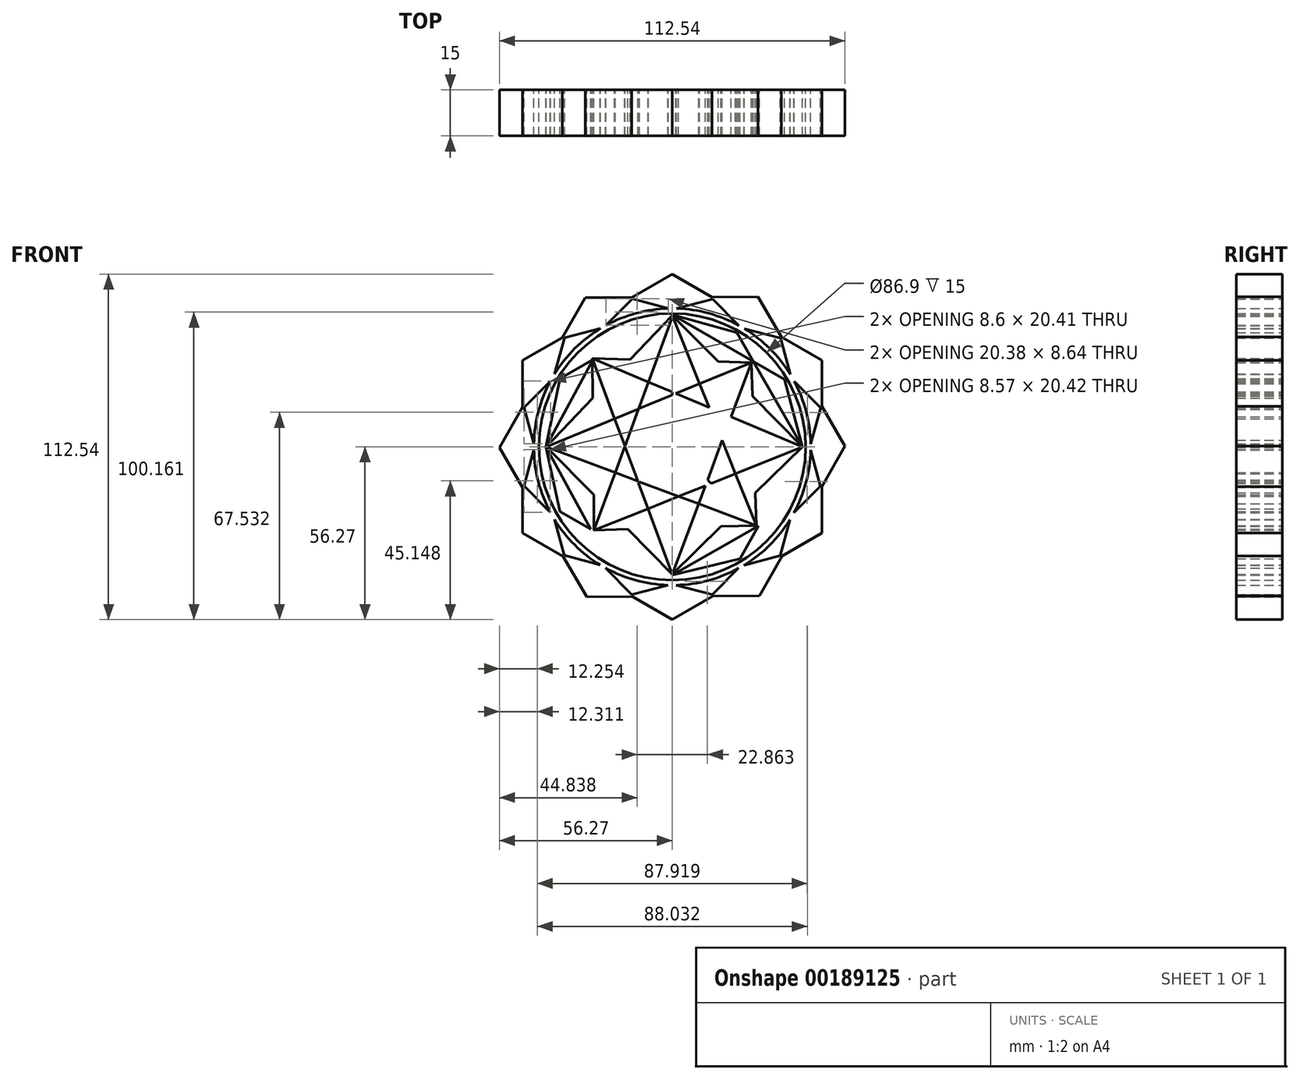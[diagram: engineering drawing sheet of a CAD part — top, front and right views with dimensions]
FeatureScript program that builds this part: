
annotation { "Feature Type Name" : "Feature", "Feature Type Description" : "" }
export const myFeature = defineFeature(function(context is Context, id is Id, definition is map)
    precondition{}
    {
        {
            var Q0;
            Q0=qCreatedBy(makeId("Front.planeOp"),FACE);
            var sketch = newSketch(context, id + "F0", { "sketchPlane" : qUnion([Q0])});
            skCircle(sketch, "E0.cCircle", {"center": v(0, 0) * mm, "radius": 48.73 * mm, "construction": true});
            skLineSegment(sketch, "E0.0", {"start": v(-48.73, -28.13) * mm, "end": v(-48.73, 28.13) * mm});
            skLineSegment(sketch, "E0.1", {"start": v(-48.73, 28.13) * mm, "end": v(0, 56.27) * mm});
            skLineSegment(sketch, "E0.2", {"start": v(0, 56.27) * mm, "end": v(48.73, 28.13) * mm});
            skLineSegment(sketch, "E0.3", {"start": v(48.73, 28.13) * mm, "end": v(48.73, -28.13) * mm});
            skLineSegment(sketch, "E0.4", {"start": v(48.73, -28.13) * mm, "end": v(0, -56.27) * mm});
            skLineSegment(sketch, "E0.5", {"start": v(0, -56.27) * mm, "end": v(-48.73, -28.13) * mm});
            skPoint(sketch, "E0.0.midPoint", {"position": v(-48.73, 0) * mm});
            skLineSegment(sketch, "E1.0", {"start": v(-56.27, -0.3) * mm, "end": v(-28.4, 48.58) * mm});
            skLineSegment(sketch, "E1.1", {"start": v(-28.4, 48.58) * mm, "end": v(27.88, 48.88) * mm});
            skLineSegment(sketch, "E1.2", {"start": v(27.88, 48.88) * mm, "end": v(56.27, 0.3) * mm});
            skLineSegment(sketch, "E1.3", {"start": v(56.27, 0.3) * mm, "end": v(28.4, -48.58) * mm});
            skLineSegment(sketch, "E1.4", {"start": v(28.4, -48.58) * mm, "end": v(-27.88, -48.88) * mm});
            skLineSegment(sketch, "E1.5", {"start": v(-27.88, -48.88) * mm, "end": v(-56.27, -0.3) * mm});
            skPoint(sketch, "E1.0.midPoint", {"position": v(-42.33, 24.14) * mm});
            skCircle(sketch, "E2.cCircle", {"center": v(0, 0) * mm, "radius": 43.25 * mm, "construction": true});
            skLineSegment(sketch, "E2.0", {"start": v(-35.24, -35.38) * mm, "end": v(-48.26, 12.83) * mm});
            skLineSegment(sketch, "E2.1", {"start": v(-48.26, 12.83) * mm, "end": v(-13.02, 48.2) * mm});
            skLineSegment(sketch, "E2.2", {"start": v(-13.02, 48.2) * mm, "end": v(35.24, 35.38) * mm});
            skLineSegment(sketch, "E2.3", {"start": v(35.24, 35.38) * mm, "end": v(48.26, -12.83) * mm});
            skLineSegment(sketch, "E2.4", {"start": v(48.26, -12.83) * mm, "end": v(13.02, -48.2) * mm});
            skLineSegment(sketch, "E2.5", {"start": v(13.02, -48.2) * mm, "end": v(-35.24, -35.38) * mm});
            skPoint(sketch, "E2.0.midPoint", {"position": v(-41.75, -11.28) * mm});
            skLineSegment(sketch, "E3.0", {"start": v(-35.12, 35.5) * mm, "end": v(13.18, 48.17) * mm});
            skLineSegment(sketch, "E3.1", {"start": v(13.18, 48.17) * mm, "end": v(48.3, 12.67) * mm});
            skLineSegment(sketch, "E3.2", {"start": v(48.3, 12.67) * mm, "end": v(35.12, -35.5) * mm});
            skLineSegment(sketch, "E3.3", {"start": v(35.12, -35.5) * mm, "end": v(-13.18, -48.17) * mm});
            skLineSegment(sketch, "E3.4", {"start": v(-13.18, -48.17) * mm, "end": v(-48.3, -12.67) * mm});
            skLineSegment(sketch, "E3.5", {"start": v(-48.3, -12.67) * mm, "end": v(-35.12, 35.5) * mm});
            skPoint(sketch, "E3.0.midPoint", {"position": v(-10.97, 41.83) * mm});
            skCircle(sketch, "E4", {"center": v(0, 0) * mm, "radius": 15.33 * mm});
            skCircle(sketch, "E5", {"center": v(0, 0) * mm, "radius": 12.97 * mm});
            skCircle(sketch, "E6", {"center": v(0, 0) * mm, "radius": 10.61 * mm});
            skCircle(sketch, "E7", {"center": v(0, 0) * mm, "radius": 8.62 * mm});
            skCircle(sketch, "E8", {"center": v(0, 0) * mm, "radius": 6.35 * mm});
            skCircle(sketch, "E9", {"center": v(0, 0) * mm, "radius": 4.5 * mm});
            skCircle(sketch, "E10", {"center": v(0, 0) * mm, "radius": 3.21 * mm});
            skCircle(sketch, "E11", {"center": v(0, 0) * mm, "radius": 1.92 * mm});
            skCircle(sketch, "E12", {"center": v(-0.12, -0.11) * mm, "radius": 17.46 * mm});
            skCircle(sketch, "E13", {"center": v(0, 0) * mm, "radius": 20.13 * mm});
            skCircle(sketch, "E14", {"center": v(0, 0) * mm, "radius": 22.24 * mm});
            skCircle(sketch, "E15", {"center": v(-0.12, -0.11) * mm, "radius": 25.75 * mm});
            skCircle(sketch, "E16", {"center": v(0, 0) * mm, "radius": 23.78 * mm});
            skCircle(sketch, "E17", {"center": v(0.21, -0.44) * mm, "radius": 27.72 * mm});
            skCircle(sketch, "E18", {"center": v(0, 0) * mm, "radius": 30.47 * mm});
            skCircle(sketch, "E19", {"center": v(0.21, -0.44) * mm, "radius": 28.46 * mm});
            skCircle(sketch, "E20", {"center": v(-0.12, -0.11) * mm, "radius": 32.96 * mm});
            skSolve(sketch);
        }
        {
            var Q0;
            Q0 = qSketchRegion(id + "F0", true);
            extrude(context, id + "F1", {"entities" : qUnion([Q0]), "depth" : 15 * mm, "offsetDistance" : 25 * mm});
        }
        {
            var Q0;
            Q0=qCreatedBy(makeId("Front.planeOp"),FACE);
            var sketch = newSketch(context, id + "F2", { "sketchPlane" : qUnion([Q0])});
            skCircle(sketch, "E21", {"center": v(0, 0) * mm, "radius": 45.1 * mm});
            skCircle(sketch, "E22", {"center": v(0, 0) * mm, "radius": 43.45 * mm});
            skSolve(sketch);
        }
        {
            var Q0;
            Q0 = qSketchRegion(id + "F2", true);
            extrude(context, id + "F3", {"entities" : qUnion([Q0]), "operationType" : NewBodyOperationType.ADD, "depth" : 15 * mm});
        }
        {
            var Q0;
            Q0=qCreatedBy(makeId("Front.planeOp"),FACE);
            var sketch = newSketch(context, id + "F4", { "sketchPlane" : qUnion([Q0])});
            skLineSegment(sketch, "E23", {"start": v(0, 43.07) * mm, "end": v(21, 37.26) * mm});
            skLineSegment(sketch, "E24", {"start": v(0, 43.07) * mm, "end": v(36.6, 21.93) * mm});
            skLineSegment(sketch, "E25", {"start": v(36.6, 21.93) * mm, "end": v(0, 43.07) * mm});
            skLineSegment(sketch, "E26", {"start": v(0, 43.07) * mm, "end": v(42.41, 0) * mm});
            skLineSegment(sketch, "E27", {"start": v(42.41, 0) * mm, "end": v(37.13, -20.61) * mm});
            skLineSegment(sketch, "E28", {"start": v(37.13, -20.61) * mm, "end": v(42.41, 0) * mm});
            skLineSegment(sketch, "E29", {"start": v(42.41, 0) * mm, "end": v(22.07, -36.47) * mm});
            skLineSegment(sketch, "E30", {"start": v(22.07, -36.47) * mm, "end": v(42.41, 0) * mm});
            skLineSegment(sketch, "E31", {"start": v(42.41, 0) * mm, "end": v(0, -41.76) * mm});
            skLineSegment(sketch, "E32", {"start": v(0, -41.76) * mm, "end": v(-21, -37) * mm});
            skLineSegment(sketch, "E33", {"start": v(-21, -37) * mm, "end": v(0, -41.76) * mm});
            skLineSegment(sketch, "E34", {"start": v(0, -41.76) * mm, "end": v(-36.6, -21.14) * mm});
            skLineSegment(sketch, "E35", {"start": v(-36.6, -21.14) * mm, "end": v(0, -41.76) * mm});
            skLineSegment(sketch, "E36", {"start": v(0, -41.76) * mm, "end": v(-41.12, 0) * mm});
            skLineSegment(sketch, "E37", {"start": v(-41.12, 0) * mm, "end": v(0, 43.07) * mm});
            skLineSegment(sketch, "E38", {"start": v(42.41, 0) * mm, "end": v(36.6, 21.93) * mm});
            skLineSegment(sketch, "E39", {"start": v(42.41, 0) * mm, "end": v(21, 37.26) * mm});
            skLineSegment(sketch, "E40", {"start": v(0, -41.76) * mm, "end": v(37.13, -20.61) * mm});
            skLineSegment(sketch, "E41", {"start": v(0, -41.76) * mm, "end": v(22.07, -36.47) * mm});
            skLineSegment(sketch, "E42", {"start": v(-41.12, 0) * mm, "end": v(-36.6, -21.14) * mm});
            skLineSegment(sketch, "E43", {"start": v(-41.12, 0) * mm, "end": v(-21, -37) * mm});
            skLineSegment(sketch, "E44", {"start": v(0, 43.07) * mm, "end": v(-21, 37.26) * mm});
            skLineSegment(sketch, "E45", {"start": v(-21, 37.26) * mm, "end": v(0, 43.07) * mm});
            skLineSegment(sketch, "E46", {"start": v(0, 43.07) * mm, "end": v(-36.6, 22.22) * mm});
            skLineSegment(sketch, "E47", {"start": v(-36.6, 22.22) * mm, "end": v(0, 43.07) * mm});
            skLineSegment(sketch, "E48", {"start": v(0, 43.07) * mm, "end": v(-41.12, 0) * mm});
            skLineSegment(sketch, "E49", {"start": v(-41.12, 0) * mm, "end": v(-36.6, 22.22) * mm});
            skLineSegment(sketch, "E50", {"start": v(-41.12, 0) * mm, "end": v(-21, 37.26) * mm});
            skSolve(sketch);
        }
        {
            var Q0;
            {var subQ0=sQuery(id+"F4.wireOp",EDGE,"E23");Q0=makeQuery(id+"F4.imprint","IMPRINT",FACE,{"disambiguationData":[TD([[makeQuery(id+"F4.imprint","IMPRINT",EDGE,{"derivedFrom":subQ0}),-1.0]])]});}
            var Q1;
            {var subQ0=sQuery(id+"F4.wireOp",EDGE,"E38");Q1=makeQuery(id+"F4.imprint","IMPRINT",FACE,{"disambiguationData":[TD([[makeQuery(id+"F4.imprint","IMPRINT",EDGE,{"derivedFrom":subQ0}),1.0]])]});}
            var Q2;
            {var subQ0=sQuery(id+"F4.wireOp",EDGE,"E28");Q2=makeQuery(id+"F4.imprint","IMPRINT",FACE,{"disambiguationData":[TD([[makeQuery(id+"F4.imprint","IMPRINT",EDGE,{"derivedFrom":subQ0}),1.0]])]});}
            var Q3;
            {var subQ0=sQuery(id+"F4.wireOp",EDGE,"E41");Q3=makeQuery(id+"F4.imprint","IMPRINT",FACE,{"disambiguationData":[TD([[makeQuery(id+"F4.imprint","IMPRINT",EDGE,{"derivedFrom":subQ0}),1.0]])]});}
            var Q4;
            {var subQ0=sQuery(id+"F4.wireOp",EDGE,"E33");Q4=makeQuery(id+"F4.imprint","IMPRINT",FACE,{"disambiguationData":[TD([[makeQuery(id+"F4.imprint","IMPRINT",EDGE,{"derivedFrom":subQ0}),1.0]])]});}
            var Q5;
            {var subQ0=sQuery(id+"F4.wireOp",EDGE,"E42");Q5=makeQuery(id+"F4.imprint","IMPRINT",FACE,{"disambiguationData":[TD([[makeQuery(id+"F4.imprint","IMPRINT",EDGE,{"derivedFrom":subQ0}),1.0]])]});}
            var Q6;
            {var subQ0=sQuery(id+"F4.wireOp",EDGE,"E45");Q6=makeQuery(id+"F4.imprint","IMPRINT",FACE,{"disambiguationData":[TD([[makeQuery(id+"F4.imprint","IMPRINT",EDGE,{"derivedFrom":subQ0}),-1.0]])]});}
            var Q7;
            {var subQ0=sQuery(id+"F4.wireOp",EDGE,"E49");Q7=makeQuery(id+"F4.imprint","IMPRINT",FACE,{"disambiguationData":[TD([[makeQuery(id+"F4.imprint","IMPRINT",EDGE,{"derivedFrom":subQ0}),-1.0]])]});}
            extrude(context, id + "F5", {"entities" : qUnion([Q0, Q1, Q2, Q3, Q4, Q5, Q6, Q7]), "depth" : 15 * mm});
        }
        {
            var Q0;
            Q0=qCreatedBy(makeId("Front.planeOp"),FACE);
            var sketch = newSketch(context, id + "F6", { "sketchPlane" : qUnion([Q0])});
            skLineSegment(sketch, "E51", {"start": v(42.41, 0) * mm, "end": v(-41.1, 0) * mm});
            skLineSegment(sketch, "E52", {"start": v(0, 42.81) * mm, "end": v(0, 0) * mm});
            skLineSegment(sketch, "E53", {"start": v(0, 0) * mm, "end": v(0, -41.49) * mm});
            skLineSegment(sketch, "E54", {"start": v(0, -41.49) * mm, "end": v(-41.1, 0) * mm});
            skLineSegment(sketch, "E55", {"start": v(-41.1, 0) * mm, "end": v(0, 42.81) * mm});
            skLineSegment(sketch, "E56", {"start": v(0, 42.81) * mm, "end": v(42.41, 0) * mm});
            skLineSegment(sketch, "E57", {"start": v(42.41, 0) * mm, "end": v(0, -41.49) * mm});
            skLineSegment(sketch, "E58", {"start": v(-26.03, 28.8) * mm, "end": v(0, 0) * mm});
            skLineSegment(sketch, "E59", {"start": v(0, 0) * mm, "end": v(27.35, -25.63) * mm});
            skLineSegment(sketch, "E60", {"start": v(27.35, -25.63) * mm, "end": v(0, 0) * mm});
            skLineSegment(sketch, "E61", {"start": v(0, 0) * mm, "end": v(25.75, 27.48) * mm});
            skLineSegment(sketch, "E62", {"start": v(25.75, 27.48) * mm, "end": v(0, 0) * mm});
            skLineSegment(sketch, "E63", {"start": v(0, 0) * mm, "end": v(-25.49, -27.2) * mm});
            skLineSegment(sketch, "E64", {"start": v(-25.49, -27.2) * mm, "end": v(-26.03, 28.8) * mm});
            skLineSegment(sketch, "E65", {"start": v(-26.03, 28.8) * mm, "end": v(25.75, 27.48) * mm});
            skLineSegment(sketch, "E66", {"start": v(25.75, 27.48) * mm, "end": v(27.35, -25.63) * mm});
            skLineSegment(sketch, "E67", {"start": v(27.35, -25.63) * mm, "end": v(-25.49, -27.2) * mm});
            skLineSegment(sketch, "E68", {"start": v(25.75, 27.48) * mm, "end": v(0, -41.49) * mm});
            skLineSegment(sketch, "E69", {"start": v(0, -41.49) * mm, "end": v(-26.03, 28.8) * mm});
            skLineSegment(sketch, "E70", {"start": v(27.35, -25.63) * mm, "end": v(0, 42.81) * mm});
            skLineSegment(sketch, "E71", {"start": v(0.13, 42.55) * mm, "end": v(-25.49, -27.2) * mm});
            skLineSegment(sketch, "E72", {"start": v(25.75, 27.48) * mm, "end": v(-41.1, 0) * mm});
            skLineSegment(sketch, "E73", {"start": v(-41.1, 0) * mm, "end": v(27.35, -25.63) * mm});
            skLineSegment(sketch, "E74", {"start": v(-26.03, 28.8) * mm, "end": v(42.41, 0) * mm});
            skLineSegment(sketch, "E75", {"start": v(42.41, 0) * mm, "end": v(-25.49, -27.2) * mm});
            skSolve(sketch);
        }
        {
            var Q0;
            {var subQ1=sQuery(id+"F6.wireOp",EDGE,"E54");var subQ3=sQuery(id+"F6.wireOp",EDGE,"E67");var subQ4=makeQuery(id+"F6.imprint","INTERSECT",VERTEX,{"derivedFrom":[subQ1,subQ3]});Q0=makeQuery(id+"F6.imprint","IMPRINT",FACE,{"disambiguationData":[TD([[makeQuery(id+"F6.imprint","IMPRINT",EDGE,{"disambiguationData":[TD([[subQ4,1.0]])],"derivedFrom":subQ3}),1.0]])]});}
            var Q1;
            {var subQ0=sQuery(id+"F6.wireOp",EDGE,"E67");var subQ1=sQuery(id+"F6.wireOp",EDGE,"E54");var subQ2=makeQuery(id+"F6.imprint","INTERSECT",VERTEX,{"derivedFrom":[subQ1,subQ0]});Q1=makeQuery(id+"F6.imprint","IMPRINT",FACE,{"disambiguationData":[TD([[makeQuery(id+"F6.imprint","IMPRINT",EDGE,{"disambiguationData":[TD([[subQ2,-1.0]])],"derivedFrom":subQ1}),1.0]])]});}
            var Q2;
            {var subQ0=sQuery(id+"F6.wireOp",EDGE,"E64");var subQ1=sQuery(id+"F6.wireOp",EDGE,"E54");var subQ2=makeQuery(id+"F6.imprint","INTERSECT",VERTEX,{"derivedFrom":[subQ1,subQ0]});Q2=makeQuery(id+"F6.imprint","IMPRINT",FACE,{"disambiguationData":[TD([[makeQuery(id+"F6.imprint","IMPRINT",EDGE,{"disambiguationData":[TD([[subQ2,1.0]])],"derivedFrom":subQ1}),1.0]])]});}
            var Q3;
            {var subQ1=sQuery(id+"F6.wireOp",EDGE,"E54");var subQ3=sQuery(id+"F6.wireOp",EDGE,"E64");var subQ4=makeQuery(id+"F6.imprint","INTERSECT",VERTEX,{"derivedFrom":[subQ1,subQ3]});Q3=makeQuery(id+"F6.imprint","IMPRINT",FACE,{"disambiguationData":[TD([[makeQuery(id+"F6.imprint","IMPRINT",EDGE,{"disambiguationData":[TD([[subQ4,-1.0]])],"derivedFrom":subQ3}),1.0]])]});}
            var Q4;
            {var subQ1=sQuery(id+"F6.wireOp",EDGE,"E55");var subQ3=sQuery(id+"F6.wireOp",EDGE,"E64");var subQ4=makeQuery(id+"F6.imprint","INTERSECT",VERTEX,{"derivedFrom":[subQ1,subQ3]});Q4=makeQuery(id+"F6.imprint","IMPRINT",FACE,{"disambiguationData":[TD([[makeQuery(id+"F6.imprint","IMPRINT",EDGE,{"disambiguationData":[TD([[subQ4,1.0]])],"derivedFrom":subQ3}),1.0]])]});}
            var Q5;
            {var subQ0=sQuery(id+"F6.wireOp",EDGE,"E64");var subQ1=sQuery(id+"F6.wireOp",EDGE,"E55");var subQ2=makeQuery(id+"F6.imprint","INTERSECT",VERTEX,{"derivedFrom":[subQ1,subQ0]});Q5=makeQuery(id+"F6.imprint","IMPRINT",FACE,{"disambiguationData":[TD([[makeQuery(id+"F6.imprint","IMPRINT",EDGE,{"disambiguationData":[TD([[subQ2,-1.0]])],"derivedFrom":subQ1}),1.0]])]});}
            var Q6;
            {var subQ0=sQuery(id+"F6.wireOp",EDGE,"E65");var subQ1=sQuery(id+"F6.wireOp",EDGE,"E55");var subQ2=makeQuery(id+"F6.imprint","INTERSECT",VERTEX,{"derivedFrom":[subQ1,subQ0]});Q6=makeQuery(id+"F6.imprint","IMPRINT",FACE,{"disambiguationData":[TD([[makeQuery(id+"F6.imprint","IMPRINT",EDGE,{"disambiguationData":[TD([[subQ2,1.0]])],"derivedFrom":subQ1}),1.0]])]});}
            var Q7;
            {var subQ0=sQuery(id+"F6.wireOp",EDGE,"E65");var subQ1=sQuery(id+"F6.wireOp",EDGE,"E56");var subQ2=makeQuery(id+"F6.imprint","INTERSECT",VERTEX,{"derivedFrom":[subQ1,subQ0]});Q7=makeQuery(id+"F6.imprint","IMPRINT",FACE,{"disambiguationData":[TD([[makeQuery(id+"F6.imprint","IMPRINT",EDGE,{"disambiguationData":[TD([[subQ2,-1.0]])],"derivedFrom":subQ1}),1.0]])]});}
            var Q8;
            {var subQ0=sQuery(id+"F6.wireOp",EDGE,"E66");var subQ1=sQuery(id+"F6.wireOp",EDGE,"E56");var subQ2=makeQuery(id+"F6.imprint","INTERSECT",VERTEX,{"derivedFrom":[subQ1,subQ0]});Q8=makeQuery(id+"F6.imprint","IMPRINT",FACE,{"disambiguationData":[TD([[makeQuery(id+"F6.imprint","IMPRINT",EDGE,{"disambiguationData":[TD([[subQ2,1.0]])],"derivedFrom":subQ1}),1.0]])]});}
            var Q9;
            {var subQ1=sQuery(id+"F6.wireOp",EDGE,"E56");var subQ3=sQuery(id+"F6.wireOp",EDGE,"E66");var subQ4=makeQuery(id+"F6.imprint","INTERSECT",VERTEX,{"derivedFrom":[subQ1,subQ3]});Q9=makeQuery(id+"F6.imprint","IMPRINT",FACE,{"disambiguationData":[TD([[makeQuery(id+"F6.imprint","IMPRINT",EDGE,{"disambiguationData":[TD([[subQ4,-1.0]])],"derivedFrom":subQ3}),1.0]])]});}
            var Q10;
            {var subQ1=sQuery(id+"F6.wireOp",EDGE,"E57");var subQ3=sQuery(id+"F6.wireOp",EDGE,"E66");var subQ4=makeQuery(id+"F6.imprint","INTERSECT",VERTEX,{"derivedFrom":[subQ1,subQ3]});Q10=makeQuery(id+"F6.imprint","IMPRINT",FACE,{"disambiguationData":[TD([[makeQuery(id+"F6.imprint","IMPRINT",EDGE,{"disambiguationData":[TD([[subQ4,1.0]])],"derivedFrom":subQ3}),1.0]])]});}
            var Q11;
            {var subQ0=sQuery(id+"F6.wireOp",EDGE,"E66");var subQ1=sQuery(id+"F6.wireOp",EDGE,"E57");var subQ2=makeQuery(id+"F6.imprint","INTERSECT",VERTEX,{"derivedFrom":[subQ1,subQ0]});Q11=makeQuery(id+"F6.imprint","IMPRINT",FACE,{"disambiguationData":[TD([[makeQuery(id+"F6.imprint","IMPRINT",EDGE,{"disambiguationData":[TD([[subQ2,-1.0]])],"derivedFrom":subQ1}),1.0]])]});}
            var Q12;
            {var subQ0=sQuery(id+"F6.wireOp",EDGE,"E67");var subQ1=sQuery(id+"F6.wireOp",EDGE,"E57");var subQ2=makeQuery(id+"F6.imprint","INTERSECT",VERTEX,{"derivedFrom":[subQ1,subQ0]});Q12=makeQuery(id+"F6.imprint","IMPRINT",FACE,{"disambiguationData":[TD([[makeQuery(id+"F6.imprint","IMPRINT",EDGE,{"disambiguationData":[TD([[subQ2,1.0]])],"derivedFrom":subQ1}),1.0]])]});}
            var Q13;
            {var subQ1=sQuery(id+"F6.wireOp",EDGE,"E57");var subQ3=sQuery(id+"F6.wireOp",EDGE,"E67");var subQ4=makeQuery(id+"F6.imprint","INTERSECT",VERTEX,{"derivedFrom":[subQ1,subQ3]});Q13=makeQuery(id+"F6.imprint","IMPRINT",FACE,{"disambiguationData":[TD([[makeQuery(id+"F6.imprint","IMPRINT",EDGE,{"disambiguationData":[TD([[subQ4,-1.0]])],"derivedFrom":subQ3}),1.0]])]});}
            var Q14;
            {var subQ0=sQuery(id+"F6.wireOp",EDGE,"E55");var subQ5=sQuery(id+"F6.wireOp",EDGE,"E65");var subQ6=makeQuery(id+"F6.imprint","INTERSECT",VERTEX,{"derivedFrom":[subQ0,subQ5]});Q14=makeQuery(id+"F6.imprint","IMPRINT",FACE,{"disambiguationData":[TD([[makeQuery(id+"F6.imprint","IMPRINT",EDGE,{"disambiguationData":[TD([[subQ6,-1.0]])],"derivedFrom":subQ5}),1.0]])]});}
            var Q15;
            {var subQ0=sQuery(id+"F6.wireOp",EDGE,"E70");var subQ3=sQuery(id+"F6.wireOp",EDGE,"E71");var subQ5=makeQuery(id+"F6.imprint","INTERSECT",VERTEX,{"derivedFrom":[subQ0,subQ3]});Q15=makeQuery(id+"F6.imprint","IMPRINT",FACE,{"disambiguationData":[TD([[makeQuery(id+"F6.imprint","IMPRINT",EDGE,{"disambiguationData":[TD([[subQ5,-1.0]])],"derivedFrom":subQ3}),-1.0]])]});}
            var Q16;
            {var subQ1=sQuery(id+"F6.wireOp",EDGE,"E56");var subQ3=sQuery(id+"F6.wireOp",EDGE,"E65");var subQ4=makeQuery(id+"F6.imprint","INTERSECT",VERTEX,{"derivedFrom":[subQ1,subQ3]});Q16=makeQuery(id+"F6.imprint","IMPRINT",FACE,{"disambiguationData":[TD([[makeQuery(id+"F6.imprint","IMPRINT",EDGE,{"disambiguationData":[TD([[subQ4,1.0]])],"derivedFrom":subQ3}),1.0]])]});}
            var Q17;
            {var subQ0=sQuery(id+"F6.wireOp",EDGE,"E67");var subQ1=sQuery(id+"F6.wireOp",EDGE,"E54");var subQ2=makeQuery(id+"F6.imprint","INTERSECT",VERTEX,{"derivedFrom":[subQ1,subQ0]});Q17=makeQuery(id+"F6.imprint","IMPRINT",FACE,{"disambiguationData":[TD([[makeQuery(id+"F6.imprint","IMPRINT",EDGE,{"disambiguationData":[TD([[subQ2,-1.0]])],"derivedFrom":subQ1}),-1.0]])]});}
            var Q18;
            {var subQ0=sQuery(id+"F6.wireOp",EDGE,"E64");var subQ1=sQuery(id+"F6.wireOp",EDGE,"E54");var subQ2=makeQuery(id+"F6.imprint","INTERSECT",VERTEX,{"derivedFrom":[subQ1,subQ0]});Q18=makeQuery(id+"F6.imprint","IMPRINT",FACE,{"disambiguationData":[TD([[makeQuery(id+"F6.imprint","IMPRINT",EDGE,{"disambiguationData":[TD([[subQ2,1.0]])],"derivedFrom":subQ1}),-1.0]])]});}
            var Q19;
            {var subQ0=sQuery(id+"F6.wireOp",EDGE,"E64");var subQ1=sQuery(id+"F6.wireOp",EDGE,"E55");var subQ2=makeQuery(id+"F6.imprint","INTERSECT",VERTEX,{"derivedFrom":[subQ1,subQ0]});Q19=makeQuery(id+"F6.imprint","IMPRINT",FACE,{"disambiguationData":[TD([[makeQuery(id+"F6.imprint","IMPRINT",EDGE,{"disambiguationData":[TD([[subQ2,-1.0]])],"derivedFrom":subQ1}),-1.0]])]});}
            var Q20;
            {var subQ0=sQuery(id+"F6.wireOp",EDGE,"E65");var subQ1=sQuery(id+"F6.wireOp",EDGE,"E55");var subQ2=makeQuery(id+"F6.imprint","INTERSECT",VERTEX,{"derivedFrom":[subQ1,subQ0]});Q20=makeQuery(id+"F6.imprint","IMPRINT",FACE,{"disambiguationData":[TD([[makeQuery(id+"F6.imprint","IMPRINT",EDGE,{"disambiguationData":[TD([[subQ2,1.0]])],"derivedFrom":subQ1}),-1.0]])]});}
            var Q21;
            {var subQ0=sQuery(id+"F6.wireOp",EDGE,"E65");var subQ1=sQuery(id+"F6.wireOp",EDGE,"E56");var subQ2=makeQuery(id+"F6.imprint","INTERSECT",VERTEX,{"derivedFrom":[subQ1,subQ0]});Q21=makeQuery(id+"F6.imprint","IMPRINT",FACE,{"disambiguationData":[TD([[makeQuery(id+"F6.imprint","IMPRINT",EDGE,{"disambiguationData":[TD([[subQ2,-1.0]])],"derivedFrom":subQ1}),-1.0]])]});}
            var Q22;
            {var subQ0=sQuery(id+"F6.wireOp",EDGE,"E66");var subQ1=sQuery(id+"F6.wireOp",EDGE,"E56");var subQ2=makeQuery(id+"F6.imprint","INTERSECT",VERTEX,{"derivedFrom":[subQ1,subQ0]});Q22=makeQuery(id+"F6.imprint","IMPRINT",FACE,{"disambiguationData":[TD([[makeQuery(id+"F6.imprint","IMPRINT",EDGE,{"disambiguationData":[TD([[subQ2,1.0]])],"derivedFrom":subQ1}),-1.0]])]});}
            var Q23;
            {var subQ0=sQuery(id+"F6.wireOp",EDGE,"E66");var subQ1=sQuery(id+"F6.wireOp",EDGE,"E57");var subQ2=makeQuery(id+"F6.imprint","INTERSECT",VERTEX,{"derivedFrom":[subQ1,subQ0]});Q23=makeQuery(id+"F6.imprint","IMPRINT",FACE,{"disambiguationData":[TD([[makeQuery(id+"F6.imprint","IMPRINT",EDGE,{"disambiguationData":[TD([[subQ2,-1.0]])],"derivedFrom":subQ1}),-1.0]])]});}
            var Q24;
            {var subQ0=sQuery(id+"F6.wireOp",EDGE,"E67");var subQ1=sQuery(id+"F6.wireOp",EDGE,"E57");var subQ2=makeQuery(id+"F6.imprint","INTERSECT",VERTEX,{"derivedFrom":[subQ1,subQ0]});Q24=makeQuery(id+"F6.imprint","IMPRINT",FACE,{"disambiguationData":[TD([[makeQuery(id+"F6.imprint","IMPRINT",EDGE,{"disambiguationData":[TD([[subQ2,1.0]])],"derivedFrom":subQ1}),-1.0]])]});}
            var Q25;
            {var subQ0=sQuery(id+"F6.wireOp",EDGE,"E74");var subQ1=sQuery(id+"F6.wireOp",EDGE,"E70");var subQ2=makeQuery(id+"F6.imprint","INTERSECT",VERTEX,{"derivedFrom":[subQ1,subQ0]});Q25=makeQuery(id+"F6.imprint","IMPRINT",FACE,{"disambiguationData":[TD([[makeQuery(id+"F6.imprint","IMPRINT",EDGE,{"disambiguationData":[TD([[subQ2,-1.0]])],"derivedFrom":subQ1}),1.0]])]});}
            var Q26;
            {var subQ0=sQuery(id+"F6.wireOp",EDGE,"E74");var subQ1=sQuery(id+"F6.wireOp",EDGE,"E52");var subQ2=makeQuery(id+"F6.imprint","INTERSECT",VERTEX,{"derivedFrom":[subQ1,subQ0]});Q26=makeQuery(id+"F6.imprint","IMPRINT",FACE,{"disambiguationData":[TD([[makeQuery(id+"F6.imprint","IMPRINT",EDGE,{"disambiguationData":[TD([[subQ2,-1.0]])],"derivedFrom":subQ1}),-1.0]])]});}
            var Q27;
            {var subQ0=sQuery(id+"F6.wireOp",EDGE,"E72");var subQ1=sQuery(id+"F6.wireOp",EDGE,"E58");var subQ2=makeQuery(id+"F6.imprint","INTERSECT",VERTEX,{"derivedFrom":[subQ1,subQ0]});Q27=makeQuery(id+"F6.imprint","IMPRINT",FACE,{"disambiguationData":[TD([[makeQuery(id+"F6.imprint","IMPRINT",EDGE,{"disambiguationData":[TD([[subQ2,-1.0]])],"derivedFrom":subQ1}),-1.0]])]});}
            var Q28;
            {var subQ0=sQuery(id+"F6.wireOp",EDGE,"E69");var subQ1=sQuery(id+"F6.wireOp",EDGE,"E51");var subQ2=makeQuery(id+"F6.imprint","INTERSECT",VERTEX,{"derivedFrom":[subQ1,subQ0]});Q28=makeQuery(id+"F6.imprint","IMPRINT",FACE,{"disambiguationData":[TD([[makeQuery(id+"F6.imprint","IMPRINT",EDGE,{"disambiguationData":[TD([[subQ2,-1.0]])],"derivedFrom":subQ1}),1.0]])]});}
            var Q29;
            {var subQ0=sQuery(id+"F6.wireOp",EDGE,"E73");var subQ5=sQuery(id+"F6.wireOp",EDGE,"E53");var subQ6=makeQuery(id+"F6.imprint","INTERSECT",VERTEX,{"derivedFrom":[subQ5,subQ0]});Q29=makeQuery(id+"F6.imprint","IMPRINT",FACE,{"disambiguationData":[TD([[makeQuery(id+"F6.imprint","IMPRINT",EDGE,{"disambiguationData":[TD([[subQ6,-1.0]])],"derivedFrom":subQ5}),-1.0]])]});}
            var Q30;
            {var subQ0=sQuery(id+"F6.wireOp",EDGE,"E75");var subQ1=sQuery(id+"F6.wireOp",EDGE,"E68");var subQ2=makeQuery(id+"F6.imprint","INTERSECT",VERTEX,{"derivedFrom":[subQ1,subQ0]});Q30=makeQuery(id+"F6.imprint","IMPRINT",FACE,{"disambiguationData":[TD([[makeQuery(id+"F6.imprint","IMPRINT",EDGE,{"disambiguationData":[TD([[subQ2,-1.0]])],"derivedFrom":subQ1}),-1.0]])]});}
            var Q31;
            {var subQ0=sQuery(id+"F6.wireOp",EDGE,"E70");var subQ1=sQuery(id+"F6.wireOp",EDGE,"E51");var subQ2=makeQuery(id+"F6.imprint","INTERSECT",VERTEX,{"derivedFrom":[subQ1,subQ0]});Q31=makeQuery(id+"F6.imprint","IMPRINT",FACE,{"disambiguationData":[TD([[makeQuery(id+"F6.imprint","IMPRINT",EDGE,{"disambiguationData":[TD([[subQ2,-1.0]])],"derivedFrom":subQ1}),1.0]])]});}
            var Q32;
            {var subQ0=sQuery(id+"F6.wireOp",EDGE,"E74");var subQ1=sQuery(id+"F6.wireOp",EDGE,"E62");var subQ2=makeQuery(id+"F6.imprint","INTERSECT",VERTEX,{"derivedFrom":[subQ1,subQ0]});Q32=makeQuery(id+"F6.imprint","IMPRINT",FACE,{"disambiguationData":[TD([[makeQuery(id+"F6.imprint","IMPRINT",EDGE,{"disambiguationData":[TD([[subQ2,-1.0]])],"derivedFrom":subQ1}),1.0]])]});}
            var Q33;
            {var subQ0=sQuery(id+"F6.wireOp",EDGE,"E70");var subQ1=sQuery(id+"F6.wireOp",EDGE,"E51");var subQ2=makeQuery(id+"F6.imprint","INTERSECT",VERTEX,{"derivedFrom":[subQ1,subQ0]});Q33=makeQuery(id+"F6.imprint","IMPRINT",FACE,{"disambiguationData":[TD([[makeQuery(id+"F6.imprint","IMPRINT",EDGE,{"disambiguationData":[TD([[subQ2,-1.0]])],"derivedFrom":subQ1}),-1.0]])]});}
            var Q34;
            {var subQ0=sQuery(id+"F6.wireOp",EDGE,"E73");var subQ1=sQuery(id+"F6.wireOp",EDGE,"E53");var subQ2=makeQuery(id+"F6.imprint","INTERSECT",VERTEX,{"derivedFrom":[subQ1,subQ0]});Q34=makeQuery(id+"F6.imprint","IMPRINT",FACE,{"disambiguationData":[TD([[makeQuery(id+"F6.imprint","IMPRINT",EDGE,{"disambiguationData":[TD([[subQ2,-1.0]])],"derivedFrom":subQ1}),1.0]])]});}
            var Q35;
            {var subQ0=sQuery(id+"F6.wireOp",EDGE,"E75");var subQ1=sQuery(id+"F6.wireOp",EDGE,"E60");var subQ2=makeQuery(id+"F6.imprint","INTERSECT",VERTEX,{"derivedFrom":[subQ1,subQ0]});Q35=makeQuery(id+"F6.imprint","IMPRINT",FACE,{"disambiguationData":[TD([[makeQuery(id+"F6.imprint","IMPRINT",EDGE,{"disambiguationData":[TD([[subQ2,-1.0]])],"derivedFrom":subQ1}),1.0]])]});}
            extrude(context, id + "F7", {"entities" : qUnion([Q0, Q1, Q2, Q3, Q4, Q5, Q6, Q7, Q8, Q9, Q10, Q11, Q12, Q13, Q14, Q15, Q16, Q17, Q18, Q19, Q20, Q21, Q22, Q23, Q24, Q25, Q26, Q27, Q28, Q29, Q30, Q31, Q32, Q33, Q34, Q35]), "depth" : 15 * mm});
        }
    });
